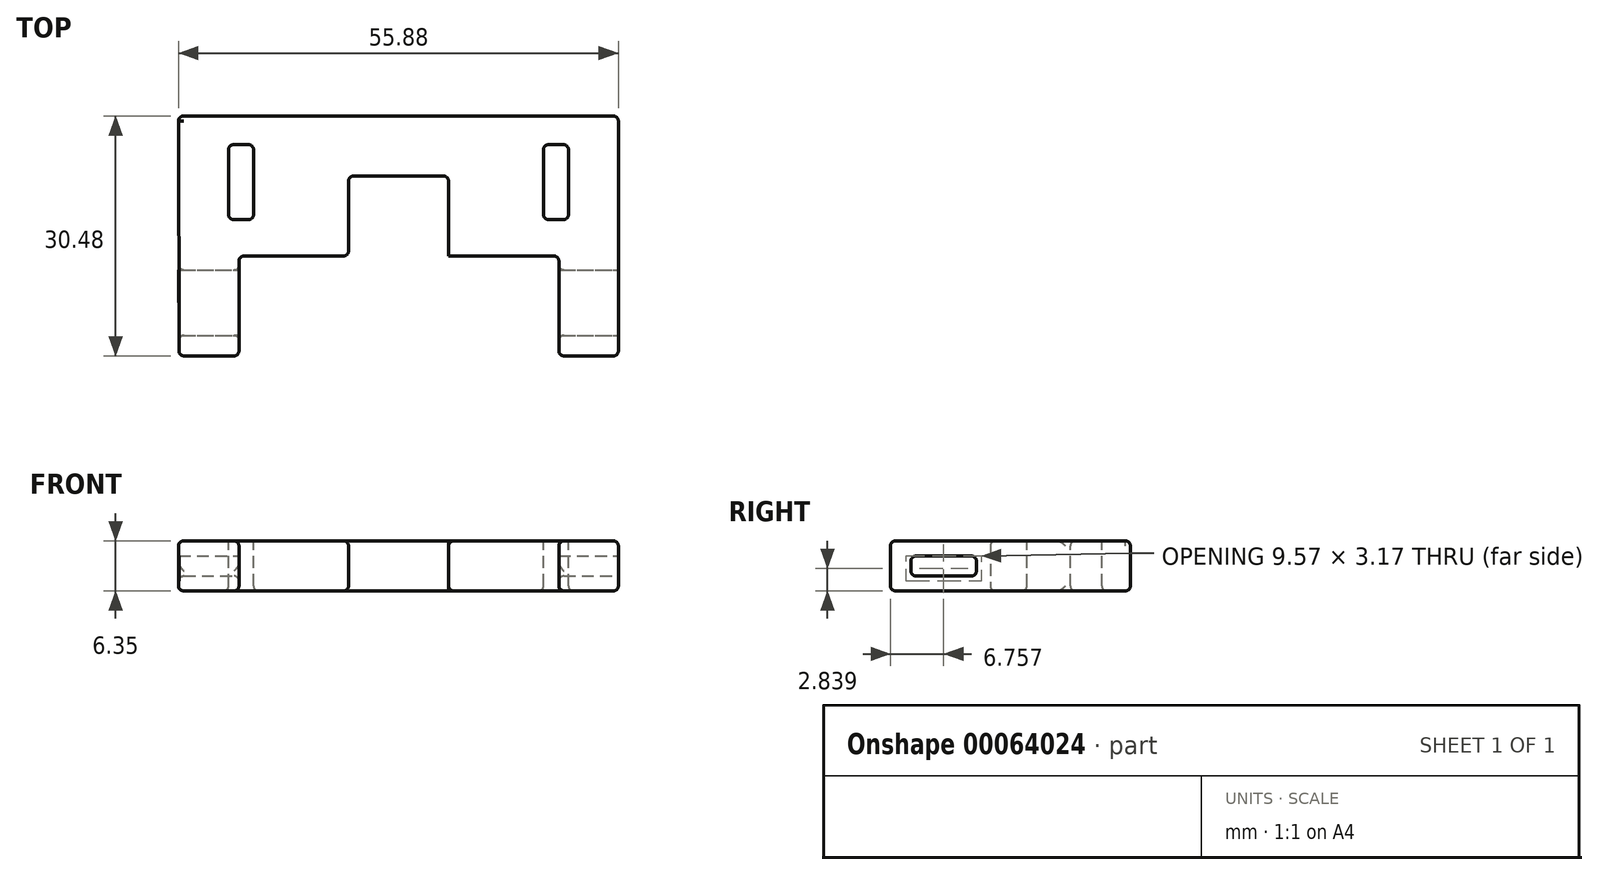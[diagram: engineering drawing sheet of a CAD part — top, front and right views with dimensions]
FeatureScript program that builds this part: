
annotation { "Feature Type Name" : "Feature", "Feature Type Description" : "" }
export const myFeature = defineFeature(function(context is Context, id is Id, definition is map)
    precondition{}
    {
        {
            var Q0;
            Q0=qCreatedBy(makeId("Top.planeOp"),FACE);
            var sketch = newSketch(context, id + "F0", { "sketchPlane" : qUnion([Q0])});
            skLineSegment(sketch, "E0", {"start": v(-44.5, 31.5) * mm, "end": v(-22.9, 31.5) * mm});
            skLineSegment(sketch, "E1", {"start": v(-22.9, 31.5) * mm, "end": v(-22.9, 31.5) * mm});
            skLineSegment(sketch, "E2", {"start": v(-22.9, 31.5) * mm, "end": v(-10.2, 31.5) * mm});
            skLineSegment(sketch, "E3", {"start": v(-10.2, 31.5) * mm, "end": v(-10.2, 31.5) * mm});
            skLineSegment(sketch, "E4", {"start": v(-10.2, 31.5) * mm, "end": v(11.39, 31.5) * mm});
            skLineSegment(sketch, "E5", {"start": v(11.39, 31.5) * mm, "end": v(11.39, 1.03) * mm});
            skLineSegment(sketch, "E6", {"start": v(11.39, 1.03) * mm, "end": v(3.83, 1.03) * mm});
            skLineSegment(sketch, "E7", {"start": v(3.83, 1.03) * mm, "end": v(3.83, 13.73) * mm});
            skLineSegment(sketch, "E8", {"start": v(3.83, 13.73) * mm, "end": v(-36.81, 13.73) * mm});
            skLineSegment(sketch, "E9", {"start": v(-36.81, 13.73) * mm, "end": v(-36.81, 1.03) * mm});
            skLineSegment(sketch, "E10", {"start": v(-36.81, 1.03) * mm, "end": v(-44.43, 1.03) * mm});
            skLineSegment(sketch, "E11", {"start": v(-44.43, 1.03) * mm, "end": v(-44.5, 31.5) * mm});
            skSolve(sketch);
        }
        {
            var Q0;
            Q0 = qSketchRegion(id + "F0", true);
            extrude(context, id + "F1", {"entities" : qUnion([Q0]), "depth" : 6.35 * mm});
        }
        {
            var Q0;
            Q0=makeQuery(id+"F1.opExtrude","CAP_FACE",FACE,{"disambiguationData":[OSD([sQuery(id+"F0.wireOp",EDGE,"E0"),sQuery(id+"F0.wireOp",EDGE,"E2"),sQuery(id+"F0.wireOp",EDGE,"E4"),sQuery(id+"F0.wireOp",EDGE,"E5"),sQuery(id+"F0.wireOp",EDGE,"E6"),sQuery(id+"F0.wireOp",EDGE,"E7"),sQuery(id+"F0.wireOp",EDGE,"E8"),sQuery(id+"F0.wireOp",EDGE,"E9"),sQuery(id+"F0.wireOp",EDGE,"E10"),sQuery(id+"F0.wireOp",EDGE,"E11")])],"isStart":false});
            var sketch = newSketch(context, id + "F2", { "sketchPlane" : qUnion([Q0])});
            skLineSegment(sketch, "E12.bottom", {"start": v(-22.89, 13.73) * mm, "end": v(-10.19, 13.73) * mm});
            skLineSegment(sketch, "E12.top", {"start": v(-22.89, 23.89) * mm, "end": v(-10.19, 23.89) * mm});
            skLineSegment(sketch, "E12.left", {"start": v(-22.89, 13.73) * mm, "end": v(-22.89, 23.89) * mm});
            skLineSegment(sketch, "E12.right", {"start": v(-10.19, 13.73) * mm, "end": v(-10.19, 23.89) * mm});
            skSolve(sketch);
        }
        {
            var Q0;
            Q0=makeQuery(id+"F2.imprint","IMPRINT",FACE,{"disambiguationData":[TD([[makeQuery(id+"F2.imprint","IMPRINT",EDGE,{"derivedFrom":sQuery(id+"F2.wireOp",EDGE,"E12.bottom")}),-1.0]])]});
            extrude(context, id + "F3", {"entities" : qUnion([Q0]), "operationType" : NewBodyOperationType.REMOVE, "oppositeDirection" : true, "depth" : 25.4 * mm});
        }
        {
            var Q0;
            Q0=makeQuery(id+"F1.opExtrude","CAP_FACE",FACE,{"disambiguationData":[OSD([sQuery(id+"F0.wireOp",EDGE,"E0"),sQuery(id+"F0.wireOp",EDGE,"E2"),sQuery(id+"F0.wireOp",EDGE,"E4"),sQuery(id+"F0.wireOp",EDGE,"E5"),sQuery(id+"F0.wireOp",EDGE,"E6"),sQuery(id+"F0.wireOp",EDGE,"E7"),sQuery(id+"F0.wireOp",EDGE,"E8"),sQuery(id+"F0.wireOp",EDGE,"E9"),sQuery(id+"F0.wireOp",EDGE,"E10"),sQuery(id+"F0.wireOp",EDGE,"E11")])],"isStart":false});
            var sketch = newSketch(context, id + "F4", { "sketchPlane" : qUnion([Q0])});
            skLineSegment(sketch, "E13.bottom", {"start": v(-38.14, 27.88) * mm, "end": v(-34.96, 27.88) * mm});
            skLineSegment(sketch, "E13.top", {"start": v(-38.14, 18.35) * mm, "end": v(-34.96, 18.35) * mm});
            skLineSegment(sketch, "E13.left", {"start": v(-38.14, 27.88) * mm, "end": v(-38.14, 18.35) * mm});
            skLineSegment(sketch, "E13.right", {"start": v(-34.96, 27.88) * mm, "end": v(-34.96, 18.35) * mm});
            skLineSegment(sketch, "E14.bottom", {"start": v(5.04, 27.88) * mm, "end": v(1.87, 27.88) * mm});
            skLineSegment(sketch, "E14.top", {"start": v(5.04, 18.35) * mm, "end": v(1.87, 18.35) * mm});
            skLineSegment(sketch, "E14.left", {"start": v(5.04, 27.88) * mm, "end": v(5.04, 18.35) * mm});
            skLineSegment(sketch, "E14.right", {"start": v(1.87, 27.88) * mm, "end": v(1.87, 18.35) * mm});
            skSolve(sketch);
        }
        {
            var Q0;
            Q0 = qSketchRegion(id + "F4", true);
            extrude(context, id + "F5", {"entities" : qUnion([Q0]), "operationType" : NewBodyOperationType.REMOVE, "oppositeDirection" : true, "depth" : 25.4 * mm});
        }
        {
            var Q0;
            Q0=makeQuery(id+"F5.boolean.opBoolean","COPY",EDGE,{"derivedFrom":makeQuery(id+"F5.opExtrude","SWEPT_EDGE",EDGE,{"disambiguationData":[OSD([sQuery(id+"F4.wireOp",EDGE,"E13.bottom"),sQuery(id+"F4.wireOp",EDGE,"E13.right")])]})});
            var Q1;
            Q1=makeQuery(id+"F5.boolean.opBoolean","COPY",EDGE,{"derivedFrom":makeQuery(id+"F5.opExtrude","SWEPT_EDGE",EDGE,{"disambiguationData":[OSD([sQuery(id+"F4.wireOp",EDGE,"E13.bottom"),sQuery(id+"F4.wireOp",EDGE,"E13.left")])]})});
            var Q2;
            Q2=makeQuery(id+"F5.boolean.opBoolean","COPY",EDGE,{"derivedFrom":makeQuery(id+"F5.opExtrude","SWEPT_EDGE",EDGE,{"disambiguationData":[OSD([sQuery(id+"F4.wireOp",EDGE,"E13.top"),sQuery(id+"F4.wireOp",EDGE,"E13.left")])]})});
            var Q3;
            Q3=makeQuery(id+"F5.boolean.opBoolean","COPY",EDGE,{"derivedFrom":makeQuery(id+"F5.opExtrude","SWEPT_EDGE",EDGE,{"disambiguationData":[OSD([sQuery(id+"F4.wireOp",EDGE,"E13.top"),sQuery(id+"F4.wireOp",EDGE,"E13.right")])]})});
            var Q4;
            Q4=makeQuery(id+"F5.boolean.opBoolean","COPY",EDGE,{"derivedFrom":makeQuery(id+"F5.opExtrude","SWEPT_EDGE",EDGE,{"disambiguationData":[OSD([sQuery(id+"F4.wireOp",EDGE,"E14.top"),sQuery(id+"F4.wireOp",EDGE,"E14.right")])]})});
            var Q5;
            Q5=makeQuery(id+"F5.boolean.opBoolean","COPY",EDGE,{"derivedFrom":makeQuery(id+"F5.opExtrude","SWEPT_EDGE",EDGE,{"disambiguationData":[OSD([sQuery(id+"F4.wireOp",EDGE,"E14.top"),sQuery(id+"F4.wireOp",EDGE,"E14.left")])]})});
            var Q6;
            Q6=makeQuery(id+"F5.boolean.opBoolean","COPY",EDGE,{"derivedFrom":makeQuery(id+"F5.opExtrude","SWEPT_EDGE",EDGE,{"disambiguationData":[OSD([sQuery(id+"F4.wireOp",EDGE,"E14.bottom"),sQuery(id+"F4.wireOp",EDGE,"E14.right")])]})});
            var Q7;
            Q7=makeQuery(id+"F5.boolean.opBoolean","COPY",EDGE,{"derivedFrom":makeQuery(id+"F5.opExtrude","SWEPT_EDGE",EDGE,{"disambiguationData":[OSD([sQuery(id+"F4.wireOp",EDGE,"E14.bottom"),sQuery(id+"F4.wireOp",EDGE,"E14.left")])]})});
            var Q8;
            Q8=makeQuery(id+"F1.opExtrude","CAP_EDGE",EDGE,{"disambiguationData":[OSD([sQuery(id+"F0.wireOp",EDGE,"E0"),sQuery(id+"F0.wireOp",EDGE,"E2"),sQuery(id+"F0.wireOp",EDGE,"E4")])],"isStart":false});
            var Q9;
            Q9=makeQuery(id+"F1.opExtrude","CAP_EDGE",EDGE,{"disambiguationData":[OSD([sQuery(id+"F0.wireOp",EDGE,"E0"),sQuery(id+"F0.wireOp",EDGE,"E2"),sQuery(id+"F0.wireOp",EDGE,"E4")])],"isStart":true});
            var Q10;
            Q10=makeQuery(id+"F1.opExtrude","CAP_EDGE",EDGE,{"disambiguationData":[OSD([sQuery(id+"F0.wireOp",EDGE,"E11")])],"isStart":false});
            var Q11;
            Q11=makeQuery(id+"F1.opExtrude","CAP_EDGE",EDGE,{"disambiguationData":[OSD([sQuery(id+"F0.wireOp",EDGE,"E11")])],"isStart":true});
            var Q12;
            Q12=makeQuery(id+"F1.opExtrude","SWEPT_EDGE",EDGE,{"disambiguationData":[OSD([sQuery(id+"F0.wireOp",EDGE,"E10"),sQuery(id+"F0.wireOp",EDGE,"E11")])]});
            var Q13;
            Q13=makeQuery(id+"F1.opExtrude","SWEPT_EDGE",EDGE,{"disambiguationData":[OSD([sQuery(id+"F0.wireOp",EDGE,"E0"),sQuery(id+"F0.wireOp",EDGE,"E11")])]});
            var Q14;
            Q14=makeQuery(id+"F1.opExtrude","SWEPT_FACE",FACE,{"disambiguationData":[OSD([sQuery(id+"F0.wireOp",EDGE,"E5")])]});
            var Q15;
            Q15=makeQuery(id+"F1.opExtrude","SWEPT_FACE",FACE,{"disambiguationData":[OSD([sQuery(id+"F0.wireOp",EDGE,"E6")])]});
            var Q16;
            Q16=makeQuery(id+"F1.opExtrude","SWEPT_FACE",FACE,{"disambiguationData":[OSD([sQuery(id+"F0.wireOp",EDGE,"E10")])]});
            var Q17;
            Q17=makeQuery(id+"F3.boolean.opBoolean","COPY",EDGE,{"derivedFrom":makeQuery(id+"F3.opExtrude","SWEPT_EDGE",EDGE,{"disambiguationData":[OSD([sQuery(id+"F0.wireOp",EDGE,"E8"),sQuery(id+"F2.wireOp",EDGE,"E12.bottom"),sQuery(id+"F2.wireOp",EDGE,"E12.left")])]})});
            var Q18;
            Q18=makeQuery(id+"F3.boolean.opBoolean","COPY",EDGE,{"derivedFrom":makeQuery(id+"F3.opExtrude","SWEPT_EDGE",EDGE,{"disambiguationData":[OSD([sQuery(id+"F0.wireOp",EDGE,"E8"),sQuery(id+"F2.wireOp",EDGE,"E12.bottom"),sQuery(id+"F2.wireOp",EDGE,"E12.right")])]})});
            fillet(context, id + "F6", {"entities" : qUnion([Q0, Q1, Q2, Q3, Q4, Q5, Q6, Q7, Q8, Q9, Q10, Q11, Q12, Q13, Q14, Q15, Q16, Q17, Q18]), "radius" : 0.64 * mm, "tangentPropagation" : true, "allowEdgeOverflow" : false});
        }
        {
            var Q0;
            Q0=makeQuery(id+"F5.boolean.opBoolean","COPY",EDGE,{"derivedFrom":makeQuery(id+"F5.opExtrude","CAP_EDGE",EDGE,{"disambiguationData":[OSD([sQuery(id+"F4.wireOp",EDGE,"E13.left")])],"isStart":true})});
            var Q1;
            Q1=makeQuery(id+"F5.boolean.opBoolean","COPY",EDGE,{"derivedFrom":makeQuery(id+"F5.opExtrude","CAP_EDGE",EDGE,{"disambiguationData":[OSD([sQuery(id+"F4.wireOp",EDGE,"E14.right")])],"isStart":true})});
            var Q2;
            Q2=makeQuery(id+"F5.boolean.opBoolean","INTERSECT",EDGE,{"derivedFrom":[makeQuery(id+"F1.opExtrude","CAP_FACE",FACE,{"disambiguationData":[OSD([sQuery(id+"F0.wireOp",EDGE,"E0"),sQuery(id+"F0.wireOp",EDGE,"E2"),sQuery(id+"F0.wireOp",EDGE,"E4"),sQuery(id+"F0.wireOp",EDGE,"E5"),sQuery(id+"F0.wireOp",EDGE,"E6"),sQuery(id+"F0.wireOp",EDGE,"E7"),sQuery(id+"F0.wireOp",EDGE,"E8"),sQuery(id+"F0.wireOp",EDGE,"E9"),sQuery(id+"F0.wireOp",EDGE,"E10"),sQuery(id+"F0.wireOp",EDGE,"E11")])],"isStart":true}),makeQuery(id+"F5.opExtrude","SWEPT_FACE",FACE,{"disambiguationData":[OSD([sQuery(id+"F4.wireOp",EDGE,"E13.right")])]})]});
            var Q3;
            Q3=makeQuery(id+"F5.boolean.opBoolean","INTERSECT",EDGE,{"derivedFrom":[makeQuery(id+"F1.opExtrude","CAP_FACE",FACE,{"disambiguationData":[OSD([sQuery(id+"F0.wireOp",EDGE,"E0"),sQuery(id+"F0.wireOp",EDGE,"E2"),sQuery(id+"F0.wireOp",EDGE,"E4"),sQuery(id+"F0.wireOp",EDGE,"E5"),sQuery(id+"F0.wireOp",EDGE,"E6"),sQuery(id+"F0.wireOp",EDGE,"E7"),sQuery(id+"F0.wireOp",EDGE,"E8"),sQuery(id+"F0.wireOp",EDGE,"E9"),sQuery(id+"F0.wireOp",EDGE,"E10"),sQuery(id+"F0.wireOp",EDGE,"E11")])],"isStart":true}),makeQuery(id+"F5.opExtrude","SWEPT_FACE",FACE,{"disambiguationData":[OSD([sQuery(id+"F4.wireOp",EDGE,"E14.right")])]})]});
            var Q4;
            {var subQ0=sQuery(id+"F0.wireOp",EDGE,"E9");var subQ1=sQuery(id+"F0.wireOp",EDGE,"E8");Q4=makeQuery(id+"F3.boolean.opBoolean","SPLIT",EDGE,{"disambiguationData":[TD([makeQuery(id+"F1.opExtrude","SWEPT_FACE",FACE,{"disambiguationData":[OSD([subQ0])]})])],"derivedFrom":makeQuery(id+"F1.opExtrude","CAP_EDGE",EDGE,{"disambiguationData":[OSD([subQ1])],"isStart":false})});}
            var Q5;
            {var subQ0=sQuery(id+"F0.wireOp",EDGE,"E9");var subQ1=sQuery(id+"F0.wireOp",EDGE,"E8");Q5=makeQuery(id+"F3.boolean.opBoolean","SPLIT",EDGE,{"disambiguationData":[TD([makeQuery(id+"F1.opExtrude","SWEPT_FACE",FACE,{"disambiguationData":[OSD([subQ0])]})])],"derivedFrom":makeQuery(id+"F1.opExtrude","CAP_EDGE",EDGE,{"disambiguationData":[OSD([subQ1])],"isStart":true})});}
            var Q6;
            {var subQ0=sQuery(id+"F0.wireOp",EDGE,"E8");var subQ1=sQuery(id+"F0.wireOp",EDGE,"E7");Q6=makeQuery(id+"F3.boolean.opBoolean","SPLIT",EDGE,{"disambiguationData":[TD([makeQuery(id+"F1.opExtrude","SWEPT_FACE",FACE,{"disambiguationData":[OSD([subQ1])]})])],"derivedFrom":makeQuery(id+"F1.opExtrude","CAP_EDGE",EDGE,{"disambiguationData":[OSD([subQ0])],"isStart":false})});}
            var Q7;
            {var subQ0=sQuery(id+"F0.wireOp",EDGE,"E8");var subQ1=sQuery(id+"F0.wireOp",EDGE,"E7");Q7=makeQuery(id+"F3.boolean.opBoolean","SPLIT",EDGE,{"disambiguationData":[TD([makeQuery(id+"F1.opExtrude","SWEPT_FACE",FACE,{"disambiguationData":[OSD([subQ1])]})])],"derivedFrom":makeQuery(id+"F1.opExtrude","CAP_EDGE",EDGE,{"disambiguationData":[OSD([subQ0])],"isStart":true})});}
            var Q8;
            Q8=makeQuery(id+"F3.boolean.opBoolean","COPY",FACE,{"derivedFrom":makeQuery(id+"F3.opExtrude","SWEPT_FACE",FACE,{"disambiguationData":[OSD([sQuery(id+"F2.wireOp",EDGE,"E12.top")])]})});
            var Q9;
            Q9=makeQuery(id+"F1.opExtrude","SWEPT_FACE",FACE,{"disambiguationData":[OSD([sQuery(id+"F0.wireOp",EDGE,"E9")])]});
            var Q10;
            Q10=makeQuery(id+"F1.opExtrude","SWEPT_FACE",FACE,{"disambiguationData":[OSD([sQuery(id+"F0.wireOp",EDGE,"E7")])]});
            fillet(context, id + "F7", {"entities" : qUnion([Q0, Q1, Q2, Q3, Q4, Q5, Q6, Q7, Q8, Q9, Q10]), "radius" : 0.64 * mm, "tangentPropagation" : true, "allowEdgeOverflow" : false});
        }
        {
            var Q0;
            Q0=makeQuery(id+"F1.opExtrude","SWEPT_FACE",FACE,{"disambiguationData":[OSD([sQuery(id+"F0.wireOp",EDGE,"E5")])]});
            var sketch = newSketch(context, id + "F8", { "sketchPlane" : qUnion([Q0])});
            skLineSegment(sketch, "E15.bottom", {"start": v(3.63, 4.43) * mm, "end": v(11.94, 4.43) * mm});
            skLineSegment(sketch, "E15.top", {"start": v(3.63, 1.89) * mm, "end": v(11.94, 1.89) * mm});
            skLineSegment(sketch, "E15.left", {"start": v(3.63, 4.43) * mm, "end": v(3.63, 1.89) * mm});
            skLineSegment(sketch, "E15.right", {"start": v(11.94, 4.43) * mm, "end": v(11.94, 1.89) * mm});
            skSolve(sketch);
        }
        {
            var Q0;
            Q0=makeQuery(id+"F8.imprint","IMPRINT",FACE,{"disambiguationData":[TD([[makeQuery(id+"F8.imprint","IMPRINT",EDGE,{"derivedFrom":sQuery(id+"F8.wireOp",EDGE,"E15.bottom")}),-1.0]])]});
            extrude(context, id + "F9", {"entities" : qUnion([Q0]), "operationType" : NewBodyOperationType.REMOVE, "endBound" : BoundingType.THROUGH_ALL, "oppositeDirection" : true, "depth" : 25.4 * mm});
        }
        {
            var Q0;
            Q0=makeQuery(id+"F9.boolean.opBoolean","COPY",EDGE,{"disambiguationData":[OD(1.0)],"derivedFrom":makeQuery(id+"F9.opExtrude","SWEPT_EDGE",EDGE,{"disambiguationData":[OSD([sQuery(id+"F8.wireOp",EDGE,"E15.top"),sQuery(id+"F8.wireOp",EDGE,"E15.right")])]})});
            var Q1;
            Q1=makeQuery(id+"F9.boolean.opBoolean","COPY",EDGE,{"disambiguationData":[OD(1.0)],"derivedFrom":makeQuery(id+"F9.opExtrude","SWEPT_EDGE",EDGE,{"disambiguationData":[OSD([sQuery(id+"F8.wireOp",EDGE,"E15.bottom"),sQuery(id+"F8.wireOp",EDGE,"E15.right")])]})});
            var Q2;
            Q2=makeQuery(id+"F9.boolean.opBoolean","COPY",EDGE,{"disambiguationData":[OD(1.0)],"derivedFrom":makeQuery(id+"F9.opExtrude","SWEPT_EDGE",EDGE,{"disambiguationData":[OSD([sQuery(id+"F8.wireOp",EDGE,"E15.top"),sQuery(id+"F8.wireOp",EDGE,"E15.left")])]})});
            var Q3;
            Q3=makeQuery(id+"F9.boolean.opBoolean","COPY",EDGE,{"disambiguationData":[OD(1.0)],"derivedFrom":makeQuery(id+"F9.opExtrude","SWEPT_EDGE",EDGE,{"disambiguationData":[OSD([sQuery(id+"F8.wireOp",EDGE,"E15.bottom"),sQuery(id+"F8.wireOp",EDGE,"E15.left")])]})});
            var Q4;
            Q4=makeQuery(id+"F9.boolean.opBoolean","COPY",EDGE,{"disambiguationData":[OD(0.0)],"derivedFrom":makeQuery(id+"F9.opExtrude","SWEPT_EDGE",EDGE,{"disambiguationData":[OSD([sQuery(id+"F8.wireOp",EDGE,"E15.bottom"),sQuery(id+"F8.wireOp",EDGE,"E15.left")])]})});
            var Q5;
            Q5=makeQuery(id+"F9.boolean.opBoolean","COPY",EDGE,{"disambiguationData":[OD(0.0)],"derivedFrom":makeQuery(id+"F9.opExtrude","SWEPT_EDGE",EDGE,{"disambiguationData":[OSD([sQuery(id+"F8.wireOp",EDGE,"E15.bottom"),sQuery(id+"F8.wireOp",EDGE,"E15.right")])]})});
            var Q6;
            Q6=makeQuery(id+"F9.boolean.opBoolean","COPY",EDGE,{"disambiguationData":[OD(0.0)],"derivedFrom":makeQuery(id+"F9.opExtrude","SWEPT_EDGE",EDGE,{"disambiguationData":[OSD([sQuery(id+"F8.wireOp",EDGE,"E15.top"),sQuery(id+"F8.wireOp",EDGE,"E15.right")])]})});
            var Q7;
            Q7=makeQuery(id+"F9.boolean.opBoolean","COPY",EDGE,{"disambiguationData":[OD(0.0)],"derivedFrom":makeQuery(id+"F9.opExtrude","SWEPT_EDGE",EDGE,{"disambiguationData":[OSD([sQuery(id+"F8.wireOp",EDGE,"E15.top"),sQuery(id+"F8.wireOp",EDGE,"E15.left")])]})});
            var Q8;
            Q8=makeQuery(id+"F9.boolean.opBoolean","INTERSECT",EDGE,{"derivedFrom":[makeQuery(id+"F1.opExtrude","SWEPT_FACE",FACE,{"disambiguationData":[OSD([sQuery(id+"F0.wireOp",EDGE,"E11")])]}),makeQuery(id+"F9.opExtrude","SWEPT_FACE",FACE,{"disambiguationData":[OSD([sQuery(id+"F8.wireOp",EDGE,"E15.top")])]})]});
            var Q9;
            Q9=makeQuery(id+"F9.boolean.opBoolean","INTERSECT",EDGE,{"derivedFrom":[makeQuery(id+"F1.opExtrude","SWEPT_FACE",FACE,{"disambiguationData":[OSD([sQuery(id+"F0.wireOp",EDGE,"E7")])]}),makeQuery(id+"F9.opExtrude","SWEPT_FACE",FACE,{"disambiguationData":[OSD([sQuery(id+"F8.wireOp",EDGE,"E15.top")])]})]});
            var Q10;
            Q10=makeQuery(id+"F9.boolean.opBoolean","INTERSECT",EDGE,{"derivedFrom":[makeQuery(id+"F1.opExtrude","SWEPT_FACE",FACE,{"disambiguationData":[OSD([sQuery(id+"F0.wireOp",EDGE,"E9")])]}),makeQuery(id+"F9.opExtrude","SWEPT_FACE",FACE,{"disambiguationData":[OSD([sQuery(id+"F8.wireOp",EDGE,"E15.top")])]})]});
            var Q11;
            Q11=makeQuery(id+"F9.boolean.opBoolean","COPY",EDGE,{"derivedFrom":makeQuery(id+"F9.opExtrude","CAP_EDGE",EDGE,{"disambiguationData":[OSD([sQuery(id+"F8.wireOp",EDGE,"E15.top")])],"isStart":true})});
            fillet(context, id + "F10", {"entities" : qUnion([Q0, Q1, Q2, Q3, Q4, Q5, Q6, Q7, Q8, Q9, Q10, Q11]), "radius" : 0.64 * mm, "tangentPropagation" : true, "allowEdgeOverflow" : false});
        }
    });
